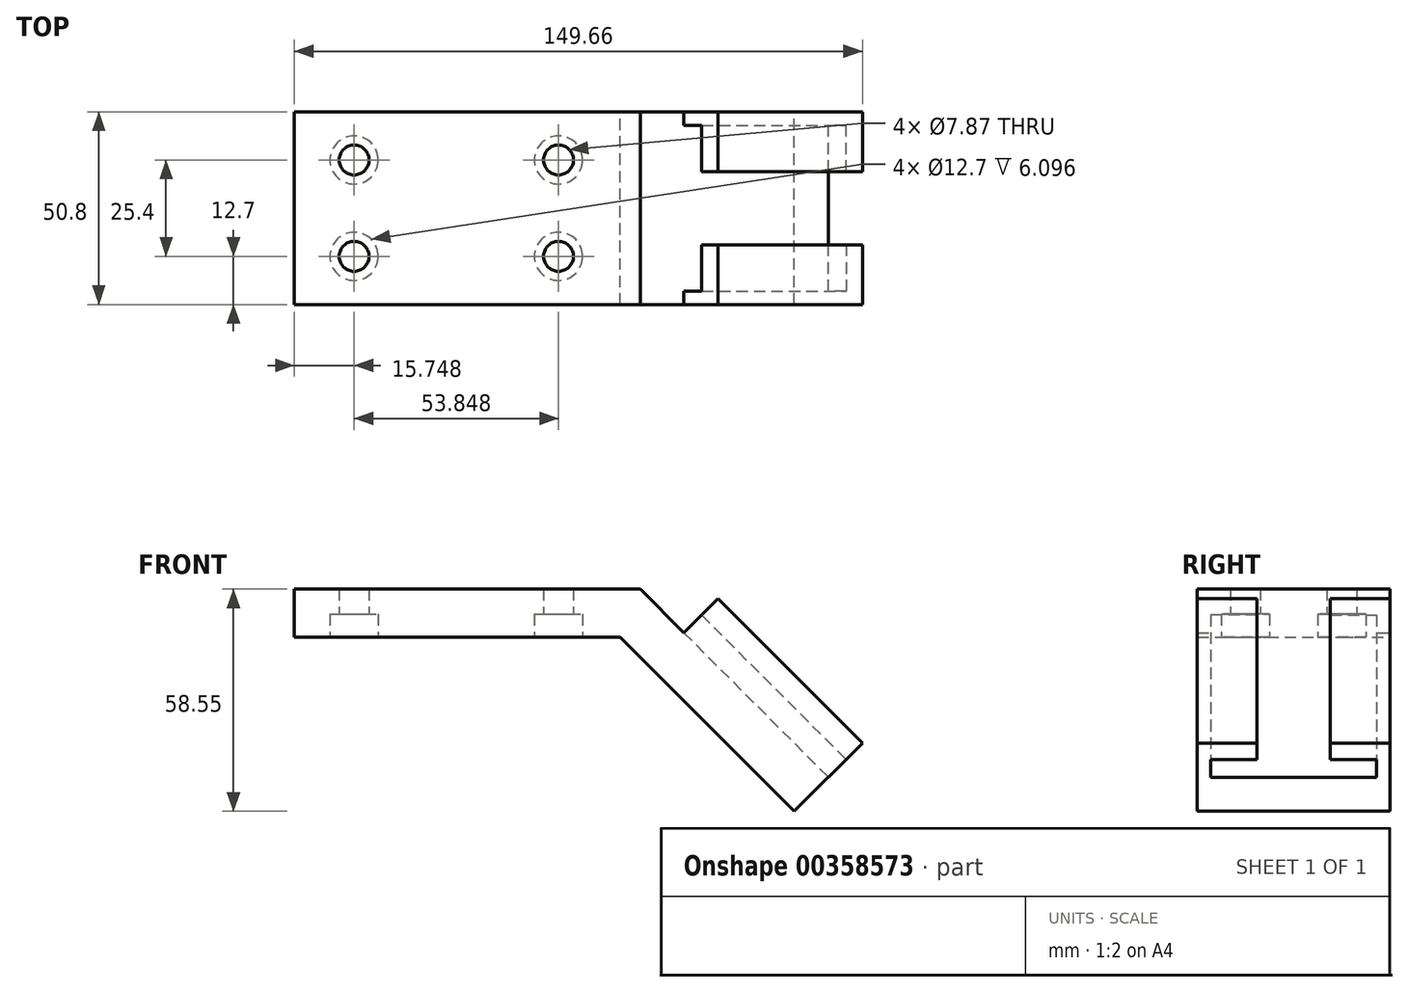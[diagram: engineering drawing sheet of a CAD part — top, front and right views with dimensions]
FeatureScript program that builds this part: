
annotation { "Feature Type Name" : "Feature", "Feature Type Description" : "" }
export const myFeature = defineFeature(function(context is Context, id is Id, definition is map)
    precondition{}
    {
        {
            var Q0;
            Q0=qCreatedBy(makeId("Front.planeOp"),FACE);
            var sketch = newSketch(context, id + "F0", { "sketchPlane" : qUnion([Q0])});
            skLineSegment(sketch, "E0", {"start": v(0, 0) * mm, "end": v(85.85, 0) * mm});
            skLineSegment(sketch, "E1", {"start": v(85.85, 0) * mm, "end": v(131.7, -45.85) * mm});
            skLineSegment(sketch, "E2", {"start": v(131.7, -45.85) * mm, "end": v(140.68, -36.87) * mm});
            skLineSegment(sketch, "E3", {"start": v(0, 0) * mm, "end": v(0, 12.7) * mm});
            skLineSegment(sketch, "E4", {"start": v(0, 12.7) * mm, "end": v(91.11, 12.7) * mm});
            skLineSegment(sketch, "E5", {"start": v(140.68, -36.87) * mm, "end": v(91.11, 12.7) * mm});
            skSolve(sketch);
        }
        {
            var Q0;
            Q0 = qSketchRegion(id + "F0", true);
            extrude(context, id + "F1", {"entities" : qUnion([Q0]), "depth" : 50.8 * mm});
        }
        {
            var Q0;
            Q0=makeQuery(id+"F1.opExtrude","SWEPT_FACE",FACE,{"disambiguationData":[OSD([sQuery(id+"F0.wireOp",EDGE,"E0")])]});
            var sketch = newSketch(context, id + "F2", { "sketchPlane" : qUnion([Q0])});
            skPoint(sketch, "E6", {"position": v(15.75, 38.1) * mm});
            skPoint(sketch, "E7", {"position": v(69.6, 38.1) * mm});
            skPoint(sketch, "E8", {"position": v(69.6, 12.7) * mm});
            skPoint(sketch, "E9", {"position": v(15.75, 12.7) * mm});
            skSolve(sketch);
        }
        {
            var Q0;
            Q0=sQuery(id+"F2.wireOp",VERTEX,"E6");
            var Q1;
            Q1=makeQuery(id+"F1.opExtrude","SWEPT_BODY",BODY,{"disambiguationData":[OSD([sQuery(id+"F0.wireOp",EDGE,"E0"),sQuery(id+"F0.wireOp",EDGE,"E1"),sQuery(id+"F0.wireOp",EDGE,"E2"),sQuery(id+"F0.wireOp",EDGE,"E3"),sQuery(id+"F0.wireOp",EDGE,"E4"),sQuery(id+"F0.wireOp",EDGE,"E5")])]});
            hole(context, id + "F3", {"style" : HoleStyle.C_BORE, "endStyle" : HoleEndStyle.THROUGH, "holeDiameter" : 7.87 * mm, "cBoreDiameter" : 12.7 * mm, "cBoreDepth" : 6.1 * mm, "isTappedThrough" : true, "tappedDepth" : 12.7 * mm, "tapClearance" : 3, "startFromSketch" : true, "locations" : qUnion([Q0]), "scope" : qUnion([Q1])});
        }
        {
            var Q0;
            Q0=sQuery(id+"F2.wireOp",VERTEX,"E7");
            var Q1;
            Q1=sQuery(id+"F2.wireOp",VERTEX,"E8");
            var Q2;
            Q2=sQuery(id+"F2.wireOp",VERTEX,"E9");
            var Q3;
            Q3=makeQuery(id+"F1.opExtrude","SWEPT_BODY",BODY,{"disambiguationData":[OSD([sQuery(id+"F0.wireOp",EDGE,"E0"),sQuery(id+"F0.wireOp",EDGE,"E1"),sQuery(id+"F0.wireOp",EDGE,"E2"),sQuery(id+"F0.wireOp",EDGE,"E3"),sQuery(id+"F0.wireOp",EDGE,"E4"),sQuery(id+"F0.wireOp",EDGE,"E5")])]});
            hole(context, id + "F4", {"style" : HoleStyle.C_BORE, "endStyle" : HoleEndStyle.THROUGH, "holeDiameter" : 7.87 * mm, "cBoreDiameter" : 12.7 * mm, "cBoreDepth" : 6.1 * mm, "isTappedThrough" : true, "tappedDepth" : 12.7 * mm, "tapClearance" : 3, "startFromSketch" : true, "locations" : qUnion([Q0, Q1, Q2]), "scope" : qUnion([Q3])});
        }
        {
            var Q0;
            Q0=makeQuery(id+"F1.opExtrude","SWEPT_FACE",FACE,{"disambiguationData":[OSD([sQuery(id+"F0.wireOp",EDGE,"E2")])]});
            var sketch = newSketch(context, id + "F5", { "sketchPlane" : qUnion([Q0])});
            skLineSegment(sketch, "E10", {"start": v(0, 73.4) * mm, "end": v(0, 86.1) * mm});
            skLineSegment(sketch, "E11", {"start": v(0, 86.1) * mm, "end": v(-15.75, 86.1) * mm});
            skLineSegment(sketch, "E12", {"start": v(-15.75, 86.1) * mm, "end": v(-15.75, 80.01) * mm});
            skLineSegment(sketch, "E13", {"start": v(-15.75, 80.01) * mm, "end": v(-3.56, 80.01) * mm});
            skLineSegment(sketch, "E14", {"start": v(-3.56, 80.01) * mm, "end": v(-3.56, 73.4) * mm});
            skLineSegment(sketch, "E15", {"start": v(-3.56, 73.4) * mm, "end": v(0, 73.4) * mm});
            skSolve(sketch);
        }
        {
            var Q0;
            Q0 = qSketchRegion(id + "F5", true);
            extrude(context, id + "F6", {"entities" : qUnion([Q0]), "operationType" : NewBodyOperationType.ADD, "oppositeDirection" : true, "depth" : 53.85 * mm});
        }
        {
            var Q0;
            Q0=makeQuery(id+"F6.boolean.opBoolean","MERGE",FACE,{"derivedFrom":[makeQuery(id+"F1.opExtrude","SWEPT_FACE",FACE,{"disambiguationData":[OSD([sQuery(id+"F0.wireOp",EDGE,"E2")])]}),makeQuery(id+"F6.opExtrude","CAP_FACE",FACE,{"disambiguationData":[OSD([sQuery(id+"F5.wireOp",EDGE,"E10"),sQuery(id+"F5.wireOp",EDGE,"E11"),sQuery(id+"F5.wireOp",EDGE,"E12"),sQuery(id+"F5.wireOp",EDGE,"E13"),sQuery(id+"F5.wireOp",EDGE,"E14"),sQuery(id+"F5.wireOp",EDGE,"E15")])],"isStart":true})]});
            var sketch = newSketch(context, id + "F7", { "sketchPlane" : qUnion([Q0])});
            skLineSegment(sketch, "E16", {"start": v(-50.8, 73.4) * mm, "end": v(-50.8, 86.1) * mm});
            skLineSegment(sketch, "E17", {"start": v(-50.8, 86.1) * mm, "end": v(-35.05, 86.1) * mm});
            skLineSegment(sketch, "E18", {"start": v(-35.05, 86.1) * mm, "end": v(-35.05, 80.01) * mm});
            skLineSegment(sketch, "E19", {"start": v(-35.05, 80.01) * mm, "end": v(-47.24, 80.01) * mm});
            skLineSegment(sketch, "E20", {"start": v(-47.24, 80.01) * mm, "end": v(-47.24, 73.4) * mm});
            skLineSegment(sketch, "E21", {"start": v(-47.24, 73.4) * mm, "end": v(-50.8, 73.4) * mm});
            skSolve(sketch);
        }
        {
            var Q0;
            Q0 = qSketchRegion(id + "F7", true);
            extrude(context, id + "F8", {"entities" : qUnion([Q0]), "operationType" : NewBodyOperationType.ADD, "oppositeDirection" : true, "depth" : 53.85 * mm});
        }
        {
            var Q0;
            Q0=makeQuery(id+"F6.opExtrude","SWEPT_FACE",FACE,{"disambiguationData":[OSD([sQuery(id+"F5.wireOp",EDGE,"E11")])]});
            var sketch = newSketch(context, id + "F9", { "sketchPlane" : qUnion([Q0])});
            skCircle(sketch, "E22", {"center": v(71.7, -25.4) * mm, "radius": 53.85 * mm});
            skLineSegment(sketch, "E23.0.0", {"start": v(125.55, -50.8) * mm, "end": v(125.55, -35.05) * mm});
            skLineSegment(sketch, "E23.0.1", {"start": v(125.55, -35.05) * mm, "end": v(71.7, -35.05) * mm});
            skLineSegment(sketch, "E23.0.2", {"start": v(71.7, -35.05) * mm, "end": v(71.7, -50.8) * mm});
            skLineSegment(sketch, "E23.0.3", {"start": v(71.7, -50.8) * mm, "end": v(125.55, -50.8) * mm});
            skLineSegment(sketch, "E24.0.0", {"start": v(125.55, -15.75) * mm, "end": v(125.55, 0) * mm});
            skLineSegment(sketch, "E24.0.1", {"start": v(125.55, 0) * mm, "end": v(71.7, 0) * mm});
            skLineSegment(sketch, "E24.0.2", {"start": v(71.7, 0) * mm, "end": v(71.7, -15.75) * mm});
            skLineSegment(sketch, "E24.0.3", {"start": v(71.7, -15.75) * mm, "end": v(125.55, -15.75) * mm});
            skLineSegment(sketch, "E25", {"start": v(71.7, -35.05) * mm, "end": v(71.7, -15.75) * mm, "construction": true});
            skLineSegment(sketch, "E26", {"start": v(125.55, -35.05) * mm, "end": v(125.55, -15.75) * mm});
            skSolve(sketch);
        }
        {
            var Q0;
            {var subQ5=sQuery(id+"F9.wireOp",EDGE,"E23.0.0");Q0=makeQuery(id+"F9.imprint","IMPRINT",FACE,{"disambiguationData":[TD([[makeQuery(id+"F9.imprint","IMPRINT",EDGE,{"derivedFrom":subQ5}),1.0]])]});}
            var Q1;
            {var subQ0=sQuery(id+"F9.wireOp",EDGE,"E26");var subQ1=sQuery(id+"F9.wireOp",EDGE,"E22");var subQ2=makeQuery(id+"F9.imprint","INTERSECT",VERTEX,{"derivedFrom":[subQ1,subQ0]});Q1=makeQuery(id+"F9.imprint","IMPRINT",FACE,{"disambiguationData":[TD([[makeQuery(id+"F9.imprint","IMPRINT",EDGE,{"disambiguationData":[TD([[subQ2,1.0]])],"derivedFrom":subQ1}),-1.0]])]});}
            var Q2;
            {var subQ0=sQuery(id+"F9.wireOp",EDGE,"E26");var subQ1=sQuery(id+"F9.wireOp",EDGE,"E22");var subQ2=makeQuery(id+"F9.imprint","INTERSECT",VERTEX,{"derivedFrom":[subQ1,subQ0]});Q2=makeQuery(id+"F9.imprint","IMPRINT",FACE,{"disambiguationData":[TD([[makeQuery(id+"F9.imprint","IMPRINT",EDGE,{"disambiguationData":[TD([[subQ2,-1.0]])],"derivedFrom":subQ1}),-1.0]])]});}
            var Q3;
            {var subQ5=sQuery(id+"F9.wireOp",EDGE,"E24.0.0");Q3=makeQuery(id+"F9.imprint","IMPRINT",FACE,{"disambiguationData":[TD([[makeQuery(id+"F9.imprint","IMPRINT",EDGE,{"derivedFrom":subQ5}),-1.0]])]});}
            extrude(context, id + "F10", {"entities" : qUnion([Q0, Q1, Q2, Q3]), "operationType" : NewBodyOperationType.REMOVE, "oppositeDirection" : true, "depth" : 25.4 * mm});
        }
    });
